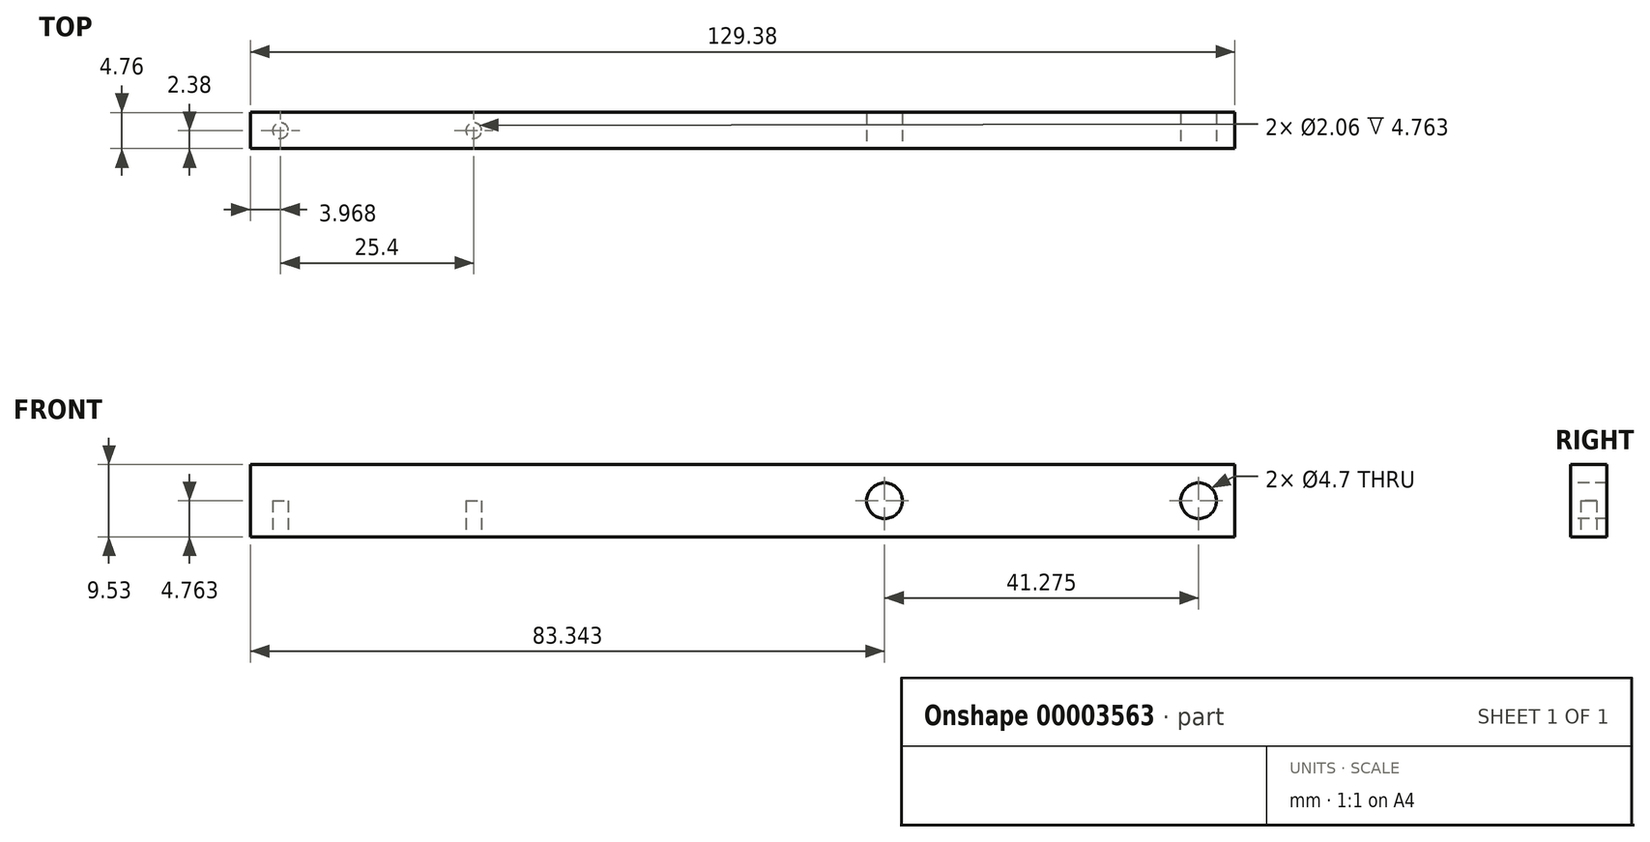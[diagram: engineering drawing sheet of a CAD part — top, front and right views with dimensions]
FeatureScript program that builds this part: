
annotation { "Feature Type Name" : "Feature", "Feature Type Description" : "" }
export const myFeature = defineFeature(function(context is Context, id is Id, definition is map)
    precondition{}
    {
        {
            var Q0;
            Q0=qCreatedBy(makeId("Top.planeOp"),FACE);
            var sketch = newSketch(context, id + "F0", { "sketchPlane" : qUnion([Q0])});
            skLineSegment(sketch, "E0.rect.bottom", {"start": v(64.7, 2.38) * mm, "end": v(-64.7, 2.38) * mm});
            skLineSegment(sketch, "E0.rect.top", {"start": v(64.7, -2.38) * mm, "end": v(-64.7, -2.38) * mm});
            skLineSegment(sketch, "E0.rect.left", {"start": v(64.7, 2.38) * mm, "end": v(64.7, -2.38) * mm});
            skLineSegment(sketch, "E0.rect.right", {"start": v(-64.7, 2.38) * mm, "end": v(-64.7, -2.38) * mm});
            skPoint(sketch, "E0.rect.middle", {"position": v(0, 0) * mm});
            skSolve(sketch);
        }
        {
            var Q0;
            Q0 = qSketchRegion(id + "F0", true);
            extrude(context, id + "F1", {"entities" : qUnion([Q0]), "depth" : 9.52 * mm});
        }
        {
            var Q0;
            Q0=makeQuery(id+"F1.opExtrude","SWEPT_FACE",FACE,{"disambiguationData":[OSD([sQuery(id+"F0.wireOp",EDGE,"E0.rect.top")])]});
            var sketch = newSketch(context, id + "F2", { "sketchPlane" : qUnion([Q0])});
            skLineSegment(sketch, "E1", {"start": v(64.7, 4.76) * mm, "end": v(18.65, 4.76) * mm, "construction": true});
            skCircle(sketch, "E2", {"center": v(18.65, 4.76) * mm, "radius": 2.35 * mm});
            skCircle(sketch, "E3", {"center": v(59.93, 4.76) * mm, "radius": 2.35 * mm});
            skSolve(sketch);
        }
        {
            var Q0;
            Q0 = qSketchRegion(id + "F2", true);
            extrude(context, id + "F3", {"entities" : qUnion([Q0]), "operationType" : NewBodyOperationType.REMOVE, "endBound" : BoundingType.THROUGH_ALL, "oppositeDirection" : true, "depth" : 25.4 * mm});
        }
        {
            var Q0;
            Q0=makeQuery(id+"F1.opExtrude","CAP_FACE",FACE,{"disambiguationData":[OSD([sQuery(id+"F0.wireOp",EDGE,"E0.rect.bottom"),sQuery(id+"F0.wireOp",EDGE,"E0.rect.top"),sQuery(id+"F0.wireOp",EDGE,"E0.rect.left"),sQuery(id+"F0.wireOp",EDGE,"E0.rect.right")])],"isStart":true});
            var sketch = newSketch(context, id + "F4", { "sketchPlane" : qUnion([Q0])});
            skLineSegment(sketch, "E4", {"start": v(-64.7, 0) * mm, "end": v(-35.32, 0) * mm, "construction": true});
            skCircle(sketch, "E5", {"center": v(-60.72, 0) * mm, "radius": 1.03 * mm});
            skCircle(sketch, "E6", {"center": v(-35.32, 0) * mm, "radius": 1.03 * mm});
            skSolve(sketch);
        }
        {
            var Q0;
            Q0 = qSketchRegion(id + "F4", true);
            extrude(context, id + "F5", {"entities" : qUnion([Q0]), "operationType" : NewBodyOperationType.REMOVE, "oppositeDirection" : true, "depth" : 4.76 * mm});
        }
    });
